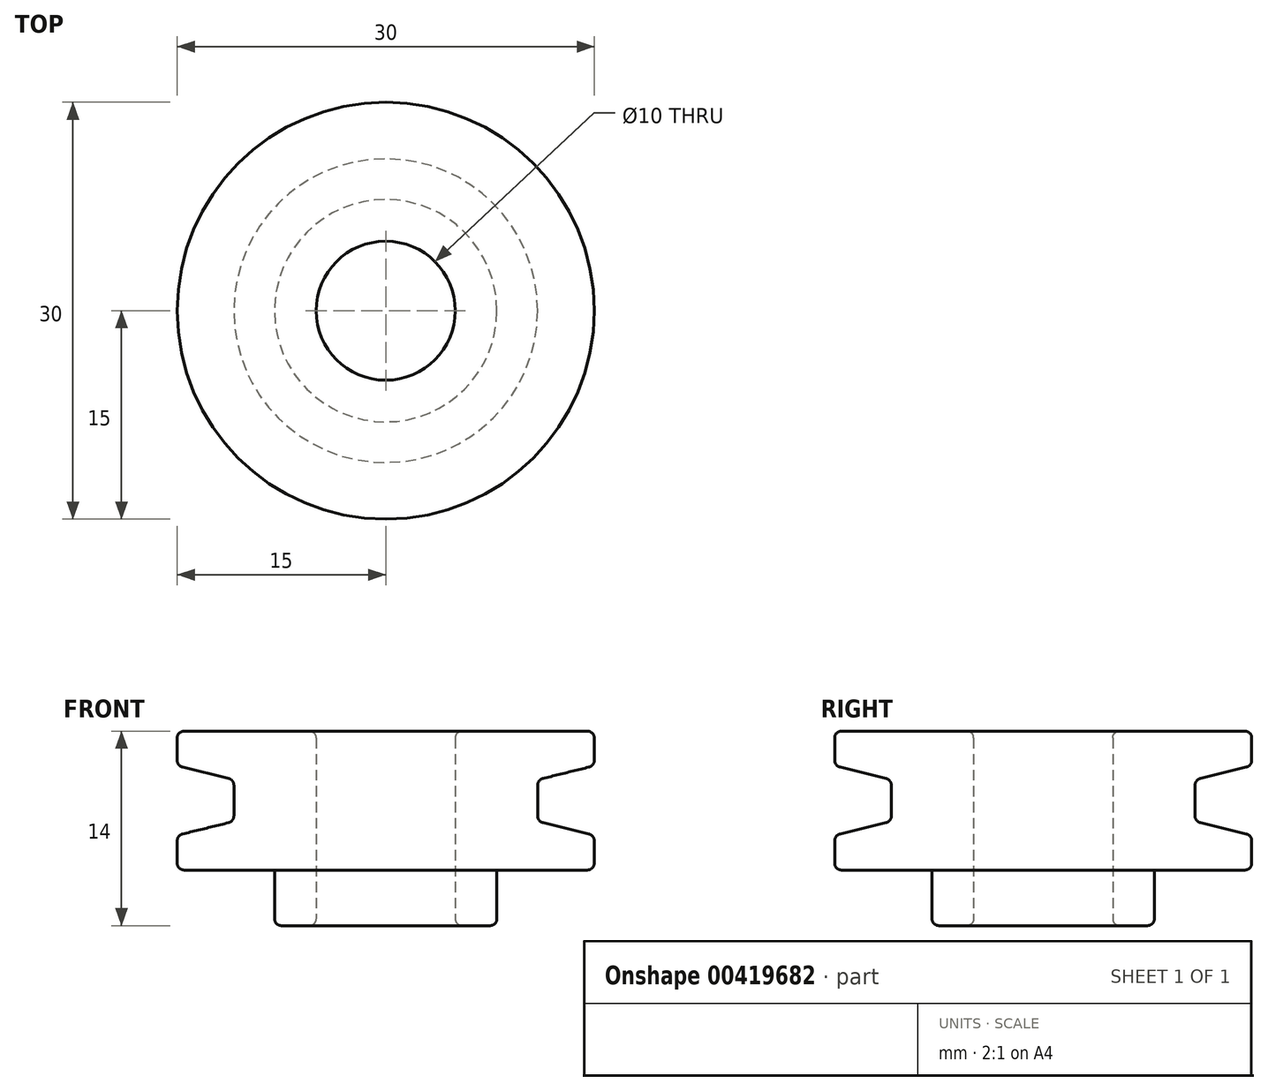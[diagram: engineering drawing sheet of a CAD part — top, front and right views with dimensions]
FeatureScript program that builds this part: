
annotation { "Feature Type Name" : "Feature", "Feature Type Description" : "" }
export const myFeature = defineFeature(function(context is Context, id is Id, definition is map)
    precondition{}
    {
        {
            var Q0;
            Q0=qCreatedBy(makeId("Front.planeOp"),FACE);
            var sketch = newSketch(context, id + "F0", { "sketchPlane" : qUnion([Q0])});
            skLineSegment(sketch, "E0", {"start": v(0, 0) * mm, "end": v(0, 10) * mm, "construction": true});
            skLineSegment(sketch, "E1", {"start": v(-5, 0) * mm, "end": v(-15, 0) * mm});
            skLineSegment(sketch, "E2", {"start": v(-15, 0) * mm, "end": v(-15, 2.5) * mm});
            skLineSegment(sketch, "E3", {"start": v(-15, 2.5) * mm, "end": v(-10.92, 3.5) * mm});
            skLineSegment(sketch, "E4", {"start": v(-10.92, 3.5) * mm, "end": v(-10.92, 6.5) * mm});
            skLineSegment(sketch, "E5", {"start": v(-10.92, 6.5) * mm, "end": v(-15, 7.5) * mm});
            skLineSegment(sketch, "E6", {"start": v(-15, 7.5) * mm, "end": v(-15, 10) * mm});
            skLineSegment(sketch, "E7", {"start": v(-15, 10) * mm, "end": v(-5, 10) * mm});
            skPoint(sketch, "E8.orphan", {"position": v(0, -27.07) * mm});
            skLineSegment(sketch, "E9", {"start": v(-5, 10) * mm, "end": v(-5, 0) * mm});
            skLineSegment(sketch, "E10", {"start": v(-5, 5) * mm, "end": v(-15.65, 5) * mm, "construction": true});
            skSolve(sketch);
        }
        {
            var Q0;
            Q0=makeQuery(id+"F0.imprint","IMPRINT",FACE,{"disambiguationData":[TD([[makeQuery(id+"F0.imprint","IMPRINT",EDGE,{"derivedFrom":sQuery(id+"F0.wireOp",EDGE,"E1")}),-1.0]])]});
            var Q1;
            Q1=sQuery(id+"F0.wireOp",EDGE,"E0");
            revolve(context, id + "F1", {"entities" : qUnion([Q0]), "axis" : qUnion([Q1]), "revolveType" : RevolveType.FULL});
        }
        {
            var Q0;
            Q0=makeQuery(id+"F1.opRevolve","SWEPT_FACE",FACE,{"disambiguationData":[OSD([sQuery(id+"F0.wireOp",EDGE,"E1")])]});
            var sketch = newSketch(context, id + "F2", { "sketchPlane" : qUnion([Q0])});
            skCircle(sketch, "E11", {"center": v(0, 0) * mm, "radius": 8 * mm});
            skSolve(sketch);
        }
        {
            var Q0;
            Q0 = qSketchRegion(id + "F2", true);
            var Q1;
            Q1=makeQuery(id+"F2.imprint","IMPRINT",FACE,{"disambiguationData":[TD([[makeQuery(id+"F2.imprint","IMPRINT",EDGE,{"derivedFrom":sQuery(id+"F2.wireOp",EDGE,"E11")}),1.0]])]});
            extrude(context, id + "F3", {"entities" : qUnion([Q0, Q1]), "operationType" : NewBodyOperationType.ADD, "depth" : 4 * mm});
        }
        {
            var Q0;
            Q0=makeQuery(id+"F3.opExtrude","CAP_FACE",FACE,{"disambiguationData":[OSD([sQuery(id+"F2.wireOp",EDGE,"E11")])],"isStart":true});
            extrude(context, id + "F4", {"entities" : qUnion([Q0]), "operationType" : NewBodyOperationType.REMOVE, "oppositeDirection" : true, "depth" : 25 * mm});
        }
        {
            var Q0;
            Q0=makeQuery(id+"F4.boolean.opBoolean","INTERSECT",EDGE,{"derivedFrom":[makeQuery(id+"F3.opExtrude","CAP_FACE",FACE,{"disambiguationData":[OSD([sQuery(id+"F2.wireOp",EDGE,"E11")])],"isStart":false}),makeQuery(id+"F4.opExtrude","SWEPT_FACE",FACE,{"disambiguationData":[OSD([sQuery(id+"F0.wireOp",EDGE,"E1"),sQuery(id+"F0.wireOp",EDGE,"E9")])]})]});
            var Q1;
            Q1=makeQuery(id+"F3.opExtrude","CAP_EDGE",EDGE,{"disambiguationData":[OSD([sQuery(id+"F2.wireOp",EDGE,"E11")])],"isStart":false});
            var Q2;
            Q2=makeQuery(id+"F3.opExtrude","CAP_EDGE",EDGE,{"disambiguationData":[OSD([sQuery(id+"F2.wireOp",EDGE,"E11")])],"isStart":true});
            var Q3;
            Q3=makeQuery(id+"F1.opRevolve","SWEPT_EDGE",EDGE,{"disambiguationData":[OSD([sQuery(id+"F0.wireOp",EDGE,"E1"),sQuery(id+"F0.wireOp",EDGE,"E2")])]});
            var Q4;
            Q4=makeQuery(id+"F1.opRevolve","SWEPT_EDGE",EDGE,{"disambiguationData":[OSD([sQuery(id+"F0.wireOp",EDGE,"E2"),sQuery(id+"F0.wireOp",EDGE,"E3")])]});
            var Q5;
            Q5=makeQuery(id+"F1.opRevolve","SWEPT_EDGE",EDGE,{"disambiguationData":[OSD([sQuery(id+"F0.wireOp",EDGE,"E5"),sQuery(id+"F0.wireOp",EDGE,"E6")])]});
            var Q6;
            Q6=makeQuery(id+"F1.opRevolve","SWEPT_EDGE",EDGE,{"disambiguationData":[OSD([sQuery(id+"F0.wireOp",EDGE,"E6"),sQuery(id+"F0.wireOp",EDGE,"E7")])]});
            var Q7;
            Q7=makeQuery(id+"F1.opRevolve","SWEPT_EDGE",EDGE,{"disambiguationData":[OSD([sQuery(id+"F0.wireOp",EDGE,"E4"),sQuery(id+"F0.wireOp",EDGE,"E5")])]});
            var Q8;
            Q8=makeQuery(id+"F1.opRevolve","SWEPT_EDGE",EDGE,{"disambiguationData":[OSD([sQuery(id+"F0.wireOp",EDGE,"E3"),sQuery(id+"F0.wireOp",EDGE,"E4")])]});
            var Q9;
            Q9=makeQuery(id+"F1.opRevolve","SWEPT_EDGE",EDGE,{"disambiguationData":[OSD([sQuery(id+"F0.wireOp",EDGE,"E7"),sQuery(id+"F0.wireOp",EDGE,"E9")])]});
            fillet(context, id + "F5", {"entities" : qUnion([Q0, Q1, Q2, Q3, Q4, Q5, Q6, Q7, Q8, Q9]), "radius" : .5 * mm, "tangentPropagation" : true, "allowEdgeOverflow" : false});
        }
    });
